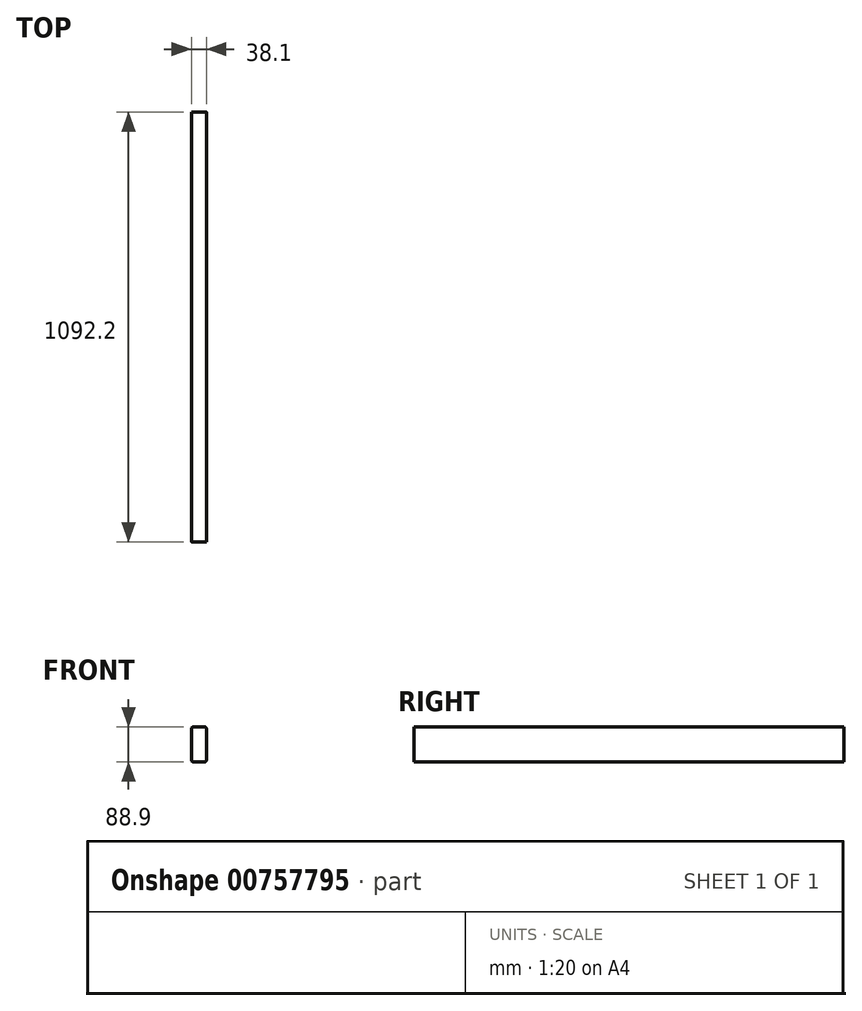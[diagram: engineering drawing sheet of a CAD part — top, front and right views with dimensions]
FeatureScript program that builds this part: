
annotation { "Feature Type Name" : "Feature", "Feature Type Description" : "" }
export const myFeature = defineFeature(function(context is Context, id is Id, definition is map)
    precondition{}
    {
        {
            var Q0;
            Q0=qCreatedBy(makeId("Front.planeOp"),FACE);
            var sketch = newSketch(context, id + "F0", { "sketchPlane" : qUnion([Q0])});
            skLineSegment(sketch, "E0.bottom", {"start": v(-32.05, 37.92) * mm, "end": v(6.05, 37.92) * mm});
            skLineSegment(sketch, "E0.top", {"start": v(-32.05, -50.98) * mm, "end": v(6.05, -50.98) * mm});
            skLineSegment(sketch, "E0.left", {"start": v(-32.05, 37.92) * mm, "end": v(-32.05, -50.98) * mm});
            skLineSegment(sketch, "E0.right", {"start": v(6.05, 37.92) * mm, "end": v(6.05, -50.98) * mm});
            skSolve(sketch);
        }
        {
            var Q0;
            Q0=makeQuery(id+"F0.imprint","IMPRINT",FACE,{"disambiguationData":[TD([[makeQuery(id+"F0.imprint","IMPRINT",EDGE,{"derivedFrom":sQuery(id+"F0.wireOp",EDGE,"E0.bottom")}),-1.0]])]});
            extrude(context, id + "F1", {"entities" : qUnion([Q0]), "depth" : 1092.2 * mm, "offsetDistance" : 25.4 * mm});
        }
        {
            var Q0;
            Q0=makeQuery(id+"F1.opExtrude","SWEPT_EDGE",EDGE,{"disambiguationData":[OSD([sQuery(id+"F0.wireOp",EDGE,"E0.bottom"),sQuery(id+"F0.wireOp",EDGE,"E0.left")])]});
            var Q1;
            Q1=makeQuery(id+"F1.opExtrude","SWEPT_EDGE",EDGE,{"disambiguationData":[OSD([sQuery(id+"F0.wireOp",EDGE,"E0.bottom"),sQuery(id+"F0.wireOp",EDGE,"E0.right")])]});
            var Q2;
            Q2=makeQuery(id+"F1.opExtrude","SWEPT_EDGE",EDGE,{"disambiguationData":[OSD([sQuery(id+"F0.wireOp",EDGE,"E0.top"),sQuery(id+"F0.wireOp",EDGE,"E0.left")])]});
            var Q3;
            Q3=makeQuery(id+"F1.opExtrude","SWEPT_EDGE",EDGE,{"disambiguationData":[OSD([sQuery(id+"F0.wireOp",EDGE,"E0.top"),sQuery(id+"F0.wireOp",EDGE,"E0.right")])]});
            fillet(context, id + "F2", {"entities" : qUnion([Q0, Q1, Q2, Q3]), "radius" : 5.08 * mm, "tangentPropagation" : true, "allowEdgeOverflow" : false});
        }
    });
